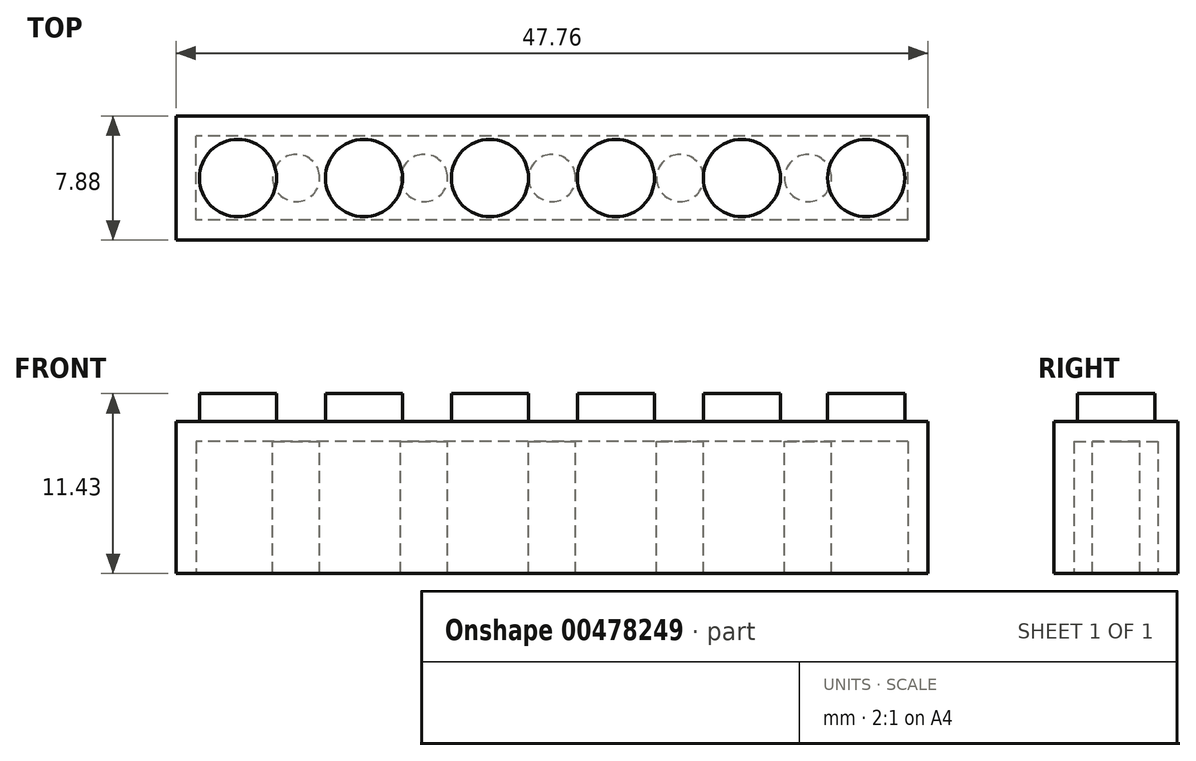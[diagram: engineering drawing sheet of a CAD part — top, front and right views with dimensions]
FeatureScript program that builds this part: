
annotation { "Feature Type Name" : "Feature", "Feature Type Description" : "" }
export const myFeature = defineFeature(function(context is Context, id is Id, definition is map)
    precondition{}
    {
        {
            var Q0;
            Q0=qCreatedBy(makeId("Top.planeOp"),FACE);
            var sketch = newSketch(context, id + "F0", { "sketchPlane" : qUnion([Q0])});
            skLineSegment(sketch, "E0.bottom", {"start": v(23.88, -3.94) * mm, "end": v(-23.88, -3.94) * mm});
            skLineSegment(sketch, "E0.top", {"start": v(23.88, 3.94) * mm, "end": v(-23.88, 3.94) * mm});
            skLineSegment(sketch, "E0.left", {"start": v(23.88, -3.94) * mm, "end": v(23.88, 3.94) * mm});
            skLineSegment(sketch, "E0.right", {"start": v(-23.88, -3.94) * mm, "end": v(-23.88, 3.94) * mm});
            skPoint(sketch, "E0.middle", {"position": v(0, 0) * mm});
            skSolve(sketch);
        }
        {
            var Q0;
            Q0 = qSketchRegion(id + "F0", true);
            extrude(context, id + "F1", {"entities" : qUnion([Q0]), "depth" : 9.65 * mm, "offsetDistance" : 25.4 * mm});
        }
        {
            var Q0;
            Q0=makeQuery(id+"F1.opExtrude","CAP_FACE",FACE,{"disambiguationData":[OSD([sQuery(id+"F0.wireOp",EDGE,"E0.bottom"),sQuery(id+"F0.wireOp",EDGE,"E0.top"),sQuery(id+"F0.wireOp",EDGE,"E0.left"),sQuery(id+"F0.wireOp",EDGE,"E0.right")])],"isStart":false});
            var sketch = newSketch(context, id + "F2", { "sketchPlane" : qUnion([Q0])});
            skCircle(sketch, "E1", {"center": v(-19.95, 0) * mm, "radius": 2.45 * mm});
            skCircle(sketch, "E2", {"center": v(-11.95, 0) * mm, "radius": 2.45 * mm});
            skCircle(sketch, "E3", {"center": v(-3.95, 0) * mm, "radius": 2.45 * mm});
            skCircle(sketch, "E4", {"center": v(4.05, 0) * mm, "radius": 2.45 * mm});
            skCircle(sketch, "E5", {"center": v(12.05, 0) * mm, "radius": 2.45 * mm});
            skCircle(sketch, "E6", {"center": v(19.95, 0) * mm, "radius": 2.45 * mm});
            skSolve(sketch);
        }
        {
            var Q0;
            Q0 = qSketchRegion(id + "F2", true);
            extrude(context, id + "F3", {"entities" : qUnion([Q0]), "operationType" : NewBodyOperationType.ADD, "depth" : 1.78 * mm, "offsetDistance" : 25.4 * mm});
        }
        {
            var Q0;
            Q0=makeQuery(id+"F1.opExtrude","CAP_FACE",FACE,{"disambiguationData":[OSD([sQuery(id+"F0.wireOp",EDGE,"E0.bottom"),sQuery(id+"F0.wireOp",EDGE,"E0.top"),sQuery(id+"F0.wireOp",EDGE,"E0.left"),sQuery(id+"F0.wireOp",EDGE,"E0.right")])],"isStart":true});
            var sketch = newSketch(context, id + "F4", { "sketchPlane" : qUnion([Q0])});
            skLineSegment(sketch, "E7.bottom", {"start": v(22.6, 2.67) * mm, "end": v(-22.6, 2.67) * mm});
            skLineSegment(sketch, "E7.top", {"start": v(22.6, -2.67) * mm, "end": v(-22.6, -2.67) * mm});
            skLineSegment(sketch, "E7.left", {"start": v(22.6, 2.67) * mm, "end": v(22.6, -2.67) * mm});
            skLineSegment(sketch, "E7.right", {"start": v(-22.6, 2.67) * mm, "end": v(-22.6, -2.67) * mm});
            skPoint(sketch, "E7.middle", {"position": v(0, 0) * mm});
            skSolve(sketch);
        }
        {
            var Q0;
            Q0 = qSketchRegion(id + "F4", true);
            extrude(context, id + "F5", {"entities" : qUnion([Q0]), "operationType" : NewBodyOperationType.REMOVE, "oppositeDirection" : true, "depth" : 8.38 * mm, "offsetDistance" : 25.4 * mm});
        }
        {
            var Q0;
            Q0=makeQuery(id+"F5.boolean.opBoolean","COPY",FACE,{"derivedFrom":makeQuery(id+"F5.opExtrude","CAP_FACE",FACE,{"disambiguationData":[OSD([sQuery(id+"F4.wireOp",EDGE,"E7.bottom"),sQuery(id+"F4.wireOp",EDGE,"E7.top"),sQuery(id+"F4.wireOp",EDGE,"E7.left"),sQuery(id+"F4.wireOp",EDGE,"E7.right")])],"isStart":false})});
            var sketch = newSketch(context, id + "F6", { "sketchPlane" : qUnion([Q0])});
            skCircle(sketch, "E8", {"center": v(-16.26, 0) * mm, "radius": 1.5 * mm});
            skCircle(sketch, "E9", {"center": v(-8.13, 0) * mm, "radius": 1.5 * mm});
            skCircle(sketch, "E10", {"center": v(0, 0) * mm, "radius": 1.5 * mm});
            skCircle(sketch, "E11", {"center": v(8.13, 0) * mm, "radius": 1.5 * mm});
            skCircle(sketch, "E12", {"center": v(16.26, 0) * mm, "radius": 1.5 * mm});
            skSolve(sketch);
        }
        {
            var Q0;
            Q0 = qSketchRegion(id + "F6", true);
            extrude(context, id + "F7", {"entities" : qUnion([Q0]), "operationType" : NewBodyOperationType.ADD, "depth" : 8.38 * mm, "offsetDistance" : 25.4 * mm});
        }
    });
